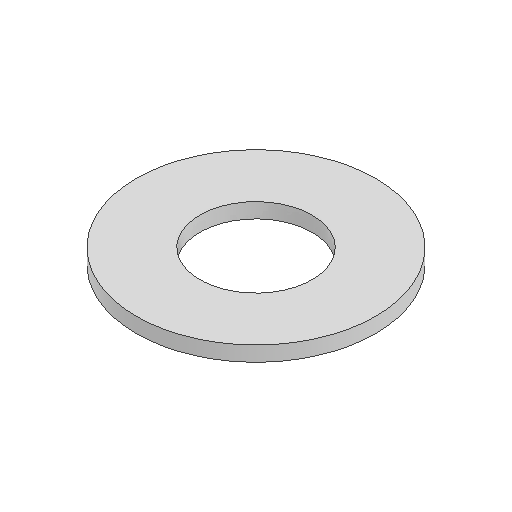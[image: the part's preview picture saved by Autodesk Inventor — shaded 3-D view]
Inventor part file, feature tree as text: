
AUTODESK INVENTOR PART (.ipt)
format: ipt  version: 2022 (Build 260153000, 153)  size: 78,848 bytes
history: native  units: in
note: dims shown in document units (in); Inventor stores cm internally (conversion verified against a paired STEP export)
features: extrude x1
ambient origin geometry x8: Origin, YZ Plane, XZ Plane, XY Plane, X Axis, Y Axis, Z Axis, Center Point
bodies: Solid1 (feature_tree)
feature tree (1):
  extrude  "Extrude1"  [1 undecoded]
note: 1 required parameter value undecoded (feature->parameter linkage not recoverable at this tier; creation-order binding heuristic only, values carry confidence <= 0.55)
